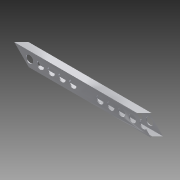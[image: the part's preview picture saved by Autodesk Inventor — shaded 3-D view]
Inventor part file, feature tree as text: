
AUTODESK INVENTOR PART (.ipt)
format: ipt  version: 2015 SP1 (Build 190203100, 203)  size: 154,624 bytes
history: native  units: in
note: dims shown in document units (in); Inventor stores cm internally (conversion verified against a paired STEP export)
features: sketch x3, hole x2, pattern_linear x2, extrude x1, fillet x1
ambient origin geometry x8: Origin, YZ Plane, XZ Plane, XY Plane, X Axis, Y Axis, Z Axis, Center Point
bodies: Solid1 (feature_tree)
feature tree (9):
  extrude  "Extrusion1"  Depth=1.0in
  fillet  "Fillet1"  Radius=1.75in
  hole  "Hole3"  [1 undecoded]
  pattern_linear  "Rectangular Pattern3"  Spacing1=21.75in  [1 undecoded]
  hole  "Hole4"  [1 undecoded]
  pattern_linear  "Rectangular Pattern4"  Spacing1=1.0in  [1 undecoded]
  sketch  "Sketch1"  dims[d0=2.0in d1=1.0in d2=1.75in]
  sketch  "Sketch4"  dims[d3=0.75in d4=0.125in]
  sketch  "Sketch5"  dims[d5=0.125in d6=21.75in d7=0.0in d32=0.125in d33=1.0in d34=3.0in d35=1.0in d36=0.75in d37=0.375in d38=0.25in d39=0.5635in d40=1.0in d41=0.8108in d42=1.9685in d44=1.5in d45=3.0in d46=1.0in d47=1.0in d48=0.75in d49=0.375in d50=0.25in d51=0.5635in d52=1.0in d53=0.8108in d54=1.9685in d56=1.5in]
note: 4 required parameter values undecoded (feature->parameter linkage not recoverable at this tier; creation-order binding heuristic only, values carry confidence <= 0.55)
